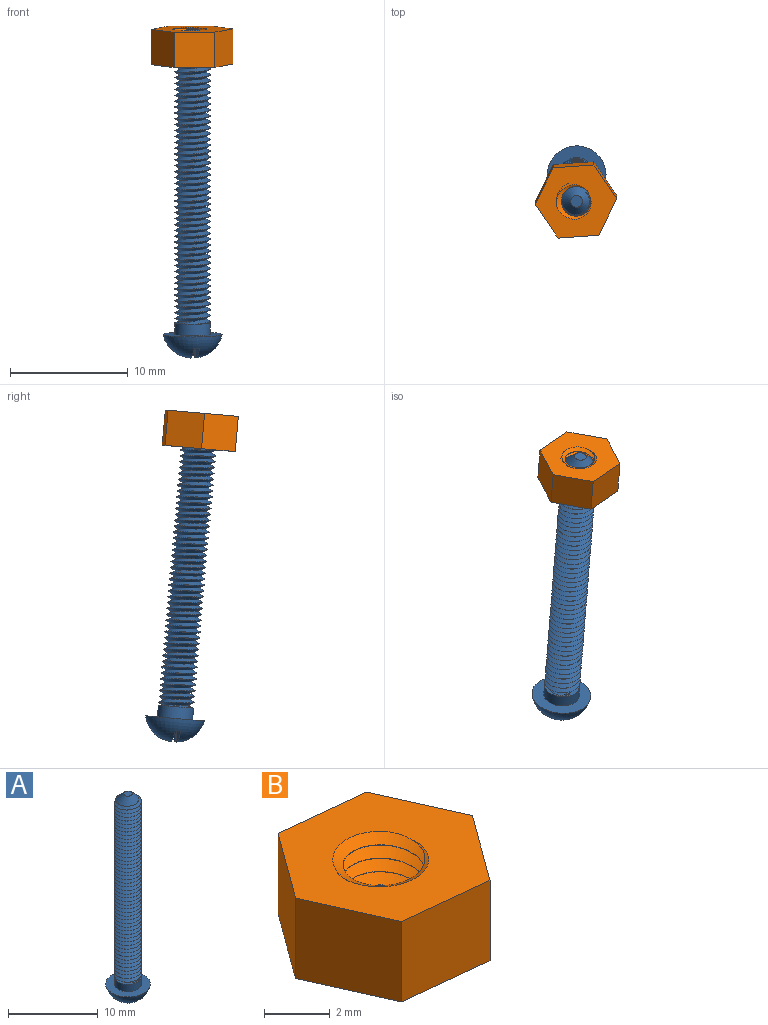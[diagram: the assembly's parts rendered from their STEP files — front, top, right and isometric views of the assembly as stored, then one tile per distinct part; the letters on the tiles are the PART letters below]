
ASSEMBLY  parts=2 mates=1
PART A: 70 faces, bbox 5.3x5.3x28.3 mm
  f0: cylinder r=1.5mm len=3mm, axis (0,0,-1), area 9.5mm2, adj f1,f52,f53,f54,f55
  f1: cylinder r=1.5mm len=3mm, axis (0,0,-1), area 0.1mm2, adj f0,f2,f52,f53
  f2: cylinder r=1.5mm len=3mm, axis (0,0,-1), area 0.1mm2, adj f1,f3,f52,f53
  f3: cylinder r=1.5mm len=3mm, axis (0,0,-1), area 0.1mm2, adj f2,f4,f52,f53
  f4: cylinder r=1.5mm len=3mm, axis (0,0,-1), area 0.1mm2, adj f3,f5,f52,f53
  f5: cylinder r=1.5mm len=3mm, axis (0,0,-1), area 0.1mm2, adj f4,f6,f52,f53
  f6: cylinder r=1.5mm len=3mm, axis (0,0,-1), area 0.1mm2, adj f5,f7,f52,f53
  f7: cylinder r=1.5mm len=3mm, axis (0,0,-1), area 0.1mm2, adj f6,f8,f52,f53
  f8: cylinder r=1.5mm len=3mm, axis (0,0,-1), area 0.1mm2, adj f7,f9,f52,f53
  f9: cylinder r=1.5mm len=3mm, axis (0,0,-1), area 0.1mm2, adj f8,f10,f52,f53
  f10: cylinder r=1.5mm len=3mm, axis (0,0,-1), area 0.1mm2, adj f9,f11,f52,f53
  f11: cylinder r=1.5mm len=3mm, axis (0,0,-1), area 0.1mm2, adj f10,f12,f52,f53
  f12: cylinder r=1.5mm len=3mm, axis (0,0,-1), area 0.1mm2, adj f11,f13,f52,f53
  f13: cylinder r=1.5mm len=3mm, axis (0,0,-1), area 0.1mm2, adj f12,f14,f52,f53
  f14: cylinder r=1.5mm len=3mm, axis (0,0,-1), area 0.1mm2, adj f13,f15,f52,f53
  f15: cylinder r=1.5mm len=3mm, axis (0,0,-1), area 0.1mm2, adj f14,f16,f52,f53
  f16: cylinder r=1.5mm len=3mm, axis (0,0,-1), area 0.1mm2, adj f15,f17,f52,f53
  f17: cylinder r=1.5mm len=3mm, axis (0,0,-1), area 0.1mm2, adj f16,f18,f52,f53
  f18: cylinder r=1.5mm len=3mm, axis (0,0,-1), area 0.1mm2, adj f17,f19,f52,f53
  f19: cylinder r=1.5mm len=3mm, axis (0,0,-1), area 0.1mm2, adj f18,f20,f52,f53
  f20: cylinder r=1.5mm len=3mm, axis (0,0,-1), area 0.1mm2, adj f19,f21,f52,f53
  f21: cylinder r=1.5mm len=3mm, axis (0,0,-1), area 0.1mm2, adj f20,f22,f52,f53
  f22: cylinder r=1.5mm len=3mm, axis (0,0,-1), area 0.1mm2, adj f21,f23,f52,f53
  f23: cylinder r=1.5mm len=3mm, axis (0,0,-1), area 0.1mm2, adj f22,f24,f52,f53
  f24: cylinder r=1.5mm len=3mm, axis (0,0,-1), area 0.1mm2, adj f23,f25,f52,f53
  f25: cylinder r=1.5mm len=3mm, axis (0,0,-1), area 0.1mm2, adj f24,f26,f52,f53
  f26: cylinder r=1.5mm len=3mm, axis (0,0,-1), area 0.1mm2, adj f25,f27,f52,f53
  f27: cylinder r=1.5mm len=3mm, axis (0,0,-1), area 0.1mm2, adj f26,f28,f52,f53
  f28: cylinder r=1.5mm len=3mm, axis (0,0,-1), area 0.1mm2, adj f27,f29,f52,f53
  f29: cylinder r=1.5mm len=3mm, axis (0,0,-1), area 0.1mm2, adj f28,f30,f52,f53
  f30: cylinder r=1.5mm len=3mm, axis (0,0,-1), area 0.1mm2, adj f29,f31,f52,f53
  f31: cylinder r=1.5mm len=3mm, axis (0,0,-1), area 0.1mm2, adj f30,f32,f52,f53
  f32: cylinder r=1.5mm len=3mm, axis (0,0,-1), area 0.1mm2, adj f31,f33,f52,f53
  f33: cylinder r=1.5mm len=3mm, axis (0,0,-1), area 0.1mm2, adj f32,f34,f52,f53
  f34: cylinder r=1.5mm len=3mm, axis (0,0,-1), area 0.1mm2, adj f33,f35,f52,f53
  f35: cylinder r=1.5mm len=3mm, axis (0,0,-1), area 0.1mm2, adj f34,f36,f52,f53
  f36: cylinder r=1.5mm len=3mm, axis (0,0,-1), area 0.1mm2, adj f35,f37,f52,f53
  f37: cylinder r=1.5mm len=3mm, axis (0,0,-1), area 0.1mm2, adj f36,f38,f52,f53
  f38: cylinder r=1.5mm len=3mm, axis (0,0,-1), area 0.1mm2, adj f37,f39,f52,f53
  f39: cylinder r=1.5mm len=3mm, axis (0,0,-1), area 0.1mm2, adj f38,f40,f52,f53
  f40: cylinder r=1.5mm len=3mm, axis (0,0,-1), area 0.1mm2, adj f39,f41,f52,f53
  f41: cylinder r=1.5mm len=3mm, axis (0,0,-1), area 0.1mm2, adj f40,f42,f52,f53
  f42: cylinder r=1.5mm len=3mm, axis (0,0,-1), area 0.1mm2, adj f41,f43,f52,f53
  f43: cylinder r=1.5mm len=3mm, axis (0,0,-1), area 0.1mm2, adj f42,f44,f52,f53
  f44: cylinder r=1.5mm len=3mm, axis (0,0,-1), area 0.1mm2, adj f43,f45,f52,f53
  f45: cylinder r=1.5mm len=3mm, axis (0,0,-1), area 0.1mm2, adj f44,f46,f52,f53
  f46: cylinder r=1.5mm len=3mm, axis (0,0,-1), area 0.1mm2, adj f45,f47,f52,f53
  f47: cylinder r=1.5mm len=3mm, axis (0,0,-1), area 0.1mm2, adj f46,f48,f52,f53
  f48: cylinder r=1.5mm len=3mm, axis (0,0,-1), area 0mm2, adj f47,f51,f52,f53
  f49: plane 1x1mm, normal (0,0,1), area 0.8mm2, adj f50
  f50: cone r=0.5mm half-angle=45deg, axis (0,0,-1), area 6.4mm2, adj f49,f51,f52,f53
  f51: cone r=0.5mm half-angle=45deg, axis (0,0,-1), area 0mm2, adj f48,f50,f52
  f52: bspline ~24.83x3.46mm, area 192.2mm2, adj f0,f1,f2,f3,f4,f5,f6,f7
  f53: bspline ~25x3.46mm, area 193.2mm2, adj f0,f1,f2,f3,f4,f5,f6,f7
  f54: plane 3.32x3.32mm, normal (0,0,1), area 1.8mm2, adj f0,f52,f53
  f55: plane 5x5mm, normal (0,0,1), area 12.6mm2, adj f0,f69
  f56: plane 1.75x0.98mm, normal (-1,0,0), area 1.2mm2, adj f57,f67,f68,f69
  f57: plane 1.75x0.98mm, normal (0,-1,0), area 1.2mm2, adj f56,f58,f68,f69
  f58: plane 0.55x0.12mm, normal (-1,0,0), area 0mm2, adj f57,f59,f68,f69
  f59: plane 1.75x0.98mm, normal (0,1,0), area 1.2mm2, adj f58,f60,f68,f69
  f60: plane 1.75x0.98mm, normal (-1,0,0), area 1.2mm2, adj f59,f61,f68,f69
  f61: plane 0.55x0.12mm, normal (0,1,0), area 0mm2, adj f60,f62,f68,f69
  f62: plane 1.75x0.98mm, normal (1,0,0), area 1.2mm2, adj f61,f63,f68,f69
  f63: plane 1.75x0.98mm, normal (0,1,0), area 1.2mm2, adj f62,f64,f68,f69
  f64: plane 0.51x0.08mm, normal (1,0,0), area 0mm2, adj f63,f65,f68,f69
  f65: plane 1.75x0.98mm, normal (0,-1,0), area 1.2mm2, adj f64,f66,f68,f69
  f66: plane 1.75x0.98mm, normal (1,0,0), area 1.2mm2, adj f65,f67,f68,f69
  f67: plane 0.55x0.12mm, normal (0,-1,0), area 0mm2, adj f56,f66,f68,f69
  f68: plane 4x4mm, normal (0,0,-1), area 3.7mm2, adj f56,f57,f58,f59,f60,f61,f62,f63
  f69: torus R=0.05mm, axis (0,0,1), area 28.2mm2, adj f55,f56,f57,f58,f59,f60,f61,f62
PART B: 11 faces, bbox 7.2x6.7x3.9 mm
  f0: cylinder r=1.25mm len=3mm, axis (0,0,1), area 0.4mm2, adj f7,f8,f9,f10
  f1: plane 3.44x3mm, normal (-0.11,-0.99,0), area 10.4mm2, adj f2,f6,f7,f8
  f2: plane 3x2.8mm, normal (0.81,-0.59,0), area 10.4mm2, adj f1,f3,f7,f8
  f3: plane 3.17x3mm, normal (0.91,0.41,0), area 10.4mm2, adj f2,f4,f7,f8
  f4: plane 3.44x3mm, normal (0.11,0.99,0), area 10.4mm2, adj f3,f5,f7,f8
  f5: plane 3x2.8mm, normal (-0.81,0.59,0), area 10.4mm2, adj f4,f6,f7,f8
  f6: plane 3.17x3mm, normal (-0.91,-0.41,0), area 10.4mm2, adj f1,f5,f7,f8
  f7: plane 7.23x6.67mm, normal (0,0,1), area 24.4mm2, adj f0,f1,f2,f3,f4,f5,f6,f9
  f8: plane 7.23x6.67mm, normal (0,0,-1), area 24.4mm2, adj f0,f1,f2,f3,f4,f5,f6,f9
  f9: bspline ~3.87x3.58mm, area 27mm2, adj f0,f7,f8,f10
  f10: bspline ~3.87x3.5mm, area 27mm2, adj f0,f7,f8,f9
PLACE A rot(axis=(0.05,0.04,-1),80.1deg) t=(-11.25,10.4,21.1)mm
PLACE B rot(axis=(0.45,-0.04,0.89),11.2deg) t=(-11.3,8.47,43.01)mm
MATE cylindrical A.f0 <-> B.f7  axis (0,-0.09,1) through (-11.25,8.22,46)mm
